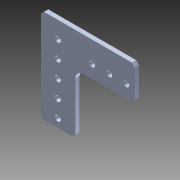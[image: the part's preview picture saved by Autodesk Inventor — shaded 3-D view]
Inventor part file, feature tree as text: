
AUTODESK INVENTOR PART (.ipt)
format: ipt  version: 2014 (Build 180170000, 170)  size: 185,344 bytes
history: native  units: in
note: dims shown in document units (in); Inventor stores cm internally (conversion verified against a paired STEP export)
features: extrude x3, sketch x3, other x2, imported_body x1
ambient origin geometry x8: Origin, YZ Plane, XZ Plane, XY Plane, X Axis, Y Axis, Z Axis, Center Point
bodies: Body1 (feature_tree)
feature tree (9):
  other  "Break-Corner1"
  other  "217-3548-STEP1"
  extrude  "Extrusion1"  Depth=1.75in
  extrude  "Extrusion2"  Depth=0.125in TaperAngle=0.0deg
  extrude  "Extrusion3"  Depth=0.125in
  imported_body  "Base1"
  sketch  "Sketch1"  dims[d0=0.035in d1=0.0in d2=1.75in]
  sketch  "Sketch2"  dims[d3=1.0in d4=0.125in d5=0.0in]
  sketch  "Sketch3"  dims[d6=0.125in d7=0.5in d8=1.1811in d10=0.5in d11=0.3937in d13=1.0in d15=0.125in d16=0.0in]
